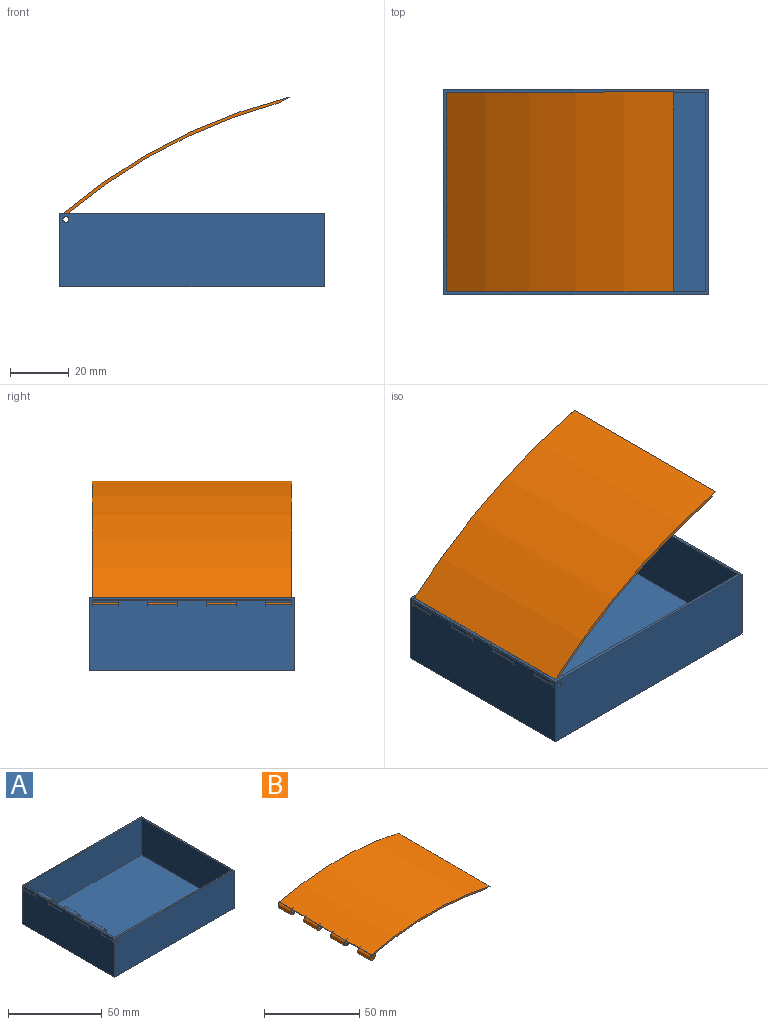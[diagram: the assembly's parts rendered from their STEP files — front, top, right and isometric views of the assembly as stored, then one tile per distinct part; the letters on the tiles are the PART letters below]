
ASSEMBLY  parts=2 mates=1
PART A: 59 faces, bbox 90x70x25 mm
  f0: plane 88x24mm, normal (0,-1,0), area 2100.9mm2, adj f1,f8,f13,f14,f20,f42,f53,f56
  f1: plane 68x20.27mm, normal (1,0,0), area 1377.8mm2, adj f0,f2,f4,f5,f6,f14,f21,f22
  f2: plane 88x24mm, normal (0,1,0), area 2100.9mm2, adj f1,f8,f13,f14,f35,f36,f52,f56
  f3: plane 70x25mm, normal (-1,0,0), area 1734.7mm2, adj f8,f10,f11,f12,f21,f22,f23,f24
  f4: cylinder r=2mm len=9.98mm, axis (0,-1,0), area 58.8mm2, adj f1,f25,f26,f33
  f5: cylinder r=2mm len=9.98mm, axis (0,-1,0), area 58.8mm2, adj f1,f23,f24,f32
  f6: cylinder r=2mm len=9.98mm, axis (0,-1,0), area 58.8mm2, adj f1,f21,f22,f34
  f7: cylinder r=1mm len=2mm, axis (0,-1,0), area 6.2mm2, adj f10,f27
  f8: plane 90x70mm, normal (0,0,1), area 312.2mm2, adj f0,f2,f3,f9,f10,f11,f19,f20
  f9: plane 70x25mm, normal (1,0,0), area 1750mm2, adj f8,f10,f11,f12
  f10: plane 90x25mm, normal (0,1,0), area 2246.9mm2, adj f3,f7,f8,f9,f12
  f11: plane 90x25mm, normal (0,-1,0), area 2246.9mm2, adj f3,f8,f9,f12,f15
  f12: plane 90x70mm, normal (0,0,-1), area 6300mm2, adj f3,f9,f10,f11
  f13: plane 68x23.99mm, normal (-1,0,0), area 1631.3mm2, adj f0,f2,f14,f56
  f14: plane 88x68mm, normal (0,0,1), area 5984mm2, adj f0,f1,f2,f13
  f15: cylinder r=1mm len=2mm, axis (0,-1,0), area 6.2mm2, adj f11,f28
  f16: cylinder r=1.99mm len=9.98mm, axis (0,1,0), area 24.1mm2, adj f21,f22,f29,f34
  f17: cylinder r=1.99mm len=9.98mm, axis (0,1,0), area 24.1mm2, adj f23,f24,f31,f32
  f18: cylinder r=1.99mm len=9.98mm, axis (0,1,0), area 24.1mm2, adj f25,f26,f30,f33
  f19: plane 68.02x0.23mm, normal (0.97,0,0.23), area 3mm2, adj f8,f27,f28,f37,f43,f49,f50,f51
  f20: cylinder r=188.99mm len=2.26mm, axis (0,1,0), area 0mm2, adj f0,f8,f27,f42
  f21: plane 4x3.99mm, normal (0,1,0), area 9.4mm2, adj f1,f3,f6,f16,f29,f34,f42,f43
  f22: plane 4x3.99mm, normal (0,-1,0), area 9.4mm2, adj f1,f3,f6,f16,f29,f34,f38,f39
  f23: plane 4x3.99mm, normal (0,1,0), area 9.4mm2, adj f1,f3,f5,f17,f31,f32,f40,f41
  f24: plane 4x3.99mm, normal (0,-1,0), area 9.4mm2, adj f1,f3,f5,f17,f31,f32,f36,f37
  f25: plane 4x3.99mm, normal (0,1,0), area 9.4mm2, adj f1,f3,f4,f18,f30,f33,f38,f39
  f26: plane 4x3.99mm, normal (0,-1,0), area 9.4mm2, adj f1,f3,f4,f18,f30,f33,f40,f41
  f27: plane 5.59x4.01mm, normal (0,-1,0), area 10.4mm2, adj f3,f7,f8,f19,f20,f42,f43
  f28: plane 5.59x4.01mm, normal (0,1,0), area 10.4mm2, adj f3,f8,f15,f19,f35,f36,f37
  f29: plane 9.98x0.01mm, normal (0.97,0,0.23), area 0.1mm2, adj f16,f21,f22,f46
  f30: plane 9.98x0.01mm, normal (0.97,0,0.23), area 0.1mm2, adj f18,f25,f26,f47
  f31: plane 9.98x0.01mm, normal (0.97,0,0.23), area 0.1mm2, adj f17,f23,f24,f48
  f32: cylinder r=188.99mm len=9.98mm, axis (0,1,0), area 0.1mm2, adj f5,f17,f23,f24
  f33: cylinder r=188.99mm len=9.98mm, axis (0,1,0), area 0.1mm2, adj f4,f18,f25,f26
  f34: cylinder r=188.99mm len=9.98mm, axis (0,1,0), area 0.1mm2, adj f6,f16,f21,f22
  f35: cylinder r=188.99mm len=2.26mm, axis (0,1,0), area 0mm2, adj f2,f8,f28,f36
  f36: cylinder r=2.01mm len=9.02mm, axis (0,-1,0), area 17.3mm2, adj f1,f2,f3,f24,f28,f35
  f37: cylinder r=2.01mm len=9.02mm, axis (0,-1,0), area 17.2mm2, adj f3,f19,f24,f28,f49,f50
  f38: cylinder r=2.01mm len=10.02mm, axis (0,-1,0), area 19.1mm2, adj f1,f3,f22,f25
  f39: cylinder r=2.01mm len=10.02mm, axis (0,-1,0), area 19.1mm2, adj f3,f22,f25,f50
  f40: cylinder r=2.01mm len=10.02mm, axis (0,-1,0), area 19.1mm2, adj f1,f3,f23,f26
  f41: cylinder r=2.01mm len=10.02mm, axis (0,-1,0), area 19.1mm2, adj f3,f23,f26,f50
  f42: cylinder r=2.01mm len=9.02mm, axis (0,-1,0), area 17.3mm2, adj f0,f1,f3,f20,f21,f27
  f43: cylinder r=2.01mm len=9.02mm, axis (0,-1,0), area 17.2mm2, adj f3,f19,f21,f27,f50,f51
  f44: cylinder r=1mm len=9.98mm, axis (0,-1,0), area 62.7mm2, adj f23,f24
  f45: cylinder r=1mm len=9.98mm, axis (0,-1,0), area 62.7mm2, adj f25,f26
  f46: cylinder r=2mm len=9.98mm, axis (0,-1,0), area 0.5mm2, adj f21,f22,f29,f50
  f47: cylinder r=2mm len=9.98mm, axis (0,-1,0), area 0.5mm2, adj f25,f26,f30,f50
  f48: cylinder r=2mm len=9.98mm, axis (0,-1,0), area 0.5mm2, adj f23,f24,f31,f50
  f49: plane 0.21x0.05mm, normal (0,1,0), area 0mm2, adj f19,f37,f50
  f50: plane 68x0.22mm, normal (1,0,0), area 14.8mm2, adj f19,f21,f22,f23,f24,f25,f26,f37
  f51: plane 0.21x0.05mm, normal (0,-1,0), area 0mm2, adj f19,f43,f50
  f52: cylinder r=188.99mm len=0.05mm, axis (0,1,0), area 0mm2, adj f2,f8,f54,f56
  f53: cylinder r=188.99mm len=0.05mm, axis (0,1,0), area 0mm2, adj f0,f8,f55,f56
  f54: plane 4.67x0.01mm, normal (0,1,0), area 0mm2, adj f8,f52,f56,f57
  f55: plane 4.67x0.01mm, normal (0,-1,0), area 0mm2, adj f8,f53,f56,f57
  f56: plane 68.02x4.63mm, normal (0,0,1), area 5.9mm2, adj f0,f2,f13,f52,f53,f54,f55,f57
  f57: cylinder r=190.01mm len=68.02mm, axis (0,1,0), area 2.9mm2, adj f8,f54,f55,f56
  f58: cylinder r=1mm len=9.98mm, axis (0,-1,0), area 62.7mm2, adj f21,f22
PART B: 23 faces, bbox 89x68x9.2 mm
  f0: cylinder r=2mm len=9mm, axis (0,-1,0), area 91.4mm2, adj f4,f5,f8,f21
  f1: cylinder r=2mm len=10mm, axis (0,-1,0), area 101.5mm2, adj f4,f5,f13,f18
  f2: cylinder r=2mm len=10mm, axis (0,-1,0), area 101.5mm2, adj f4,f5,f14,f20
  f3: cylinder r=1mm len=9mm, axis (0,-1,0), area 56.5mm2, adj f8,f21
  f4: cylinder r=189mm len=81.15mm, axis (0,1,0), area 5561.4mm2, adj f0,f1,f2,f6,f7,f8,f10,f12
  f5: plane 68x0.24mm, normal (-0.97,0,-0.23), area 16.5mm2, adj f0,f1,f2,f6,f8,f9,f10,f12
  f6: plane 89x9.17mm, normal (0,-1,0), area 94.5mm2, adj f4,f5,f7,f9,f10,f11
  f7: plane 68x4.54mm, normal (0,0,-1), area 308.8mm2, adj f4,f6,f8,f9
  f8: plane 89x9.17mm, normal (0,1,0), area 94.5mm2, adj f0,f3,f4,f5,f7,f9
  f9: cylinder r=190mm len=88mm, axis (0,1,0), area 6038.8mm2, adj f5,f6,f7,f8
  f10: cylinder r=2mm len=9mm, axis (0,-1,0), area 91.4mm2, adj f4,f5,f6,f17
  f11: cylinder r=1mm len=9mm, axis (0,-1,0), area 56.5mm2, adj f6,f17
  f12: cylinder r=2mm len=10mm, axis (0,1,0), area 24.1mm2, adj f4,f5,f13,f14
  f13: plane 4x4mm, normal (0,1,0), area 9.4mm2, adj f1,f12,f15
  f14: plane 4x4mm, normal (0,-1,0), area 9.4mm2, adj f2,f12,f22
  f15: cylinder r=1mm len=10mm, axis (0,-1,0), area 62.8mm2, adj f13,f18
  f16: cylinder r=2mm len=10mm, axis (0,1,0), area 24.1mm2, adj f4,f5,f17,f18
  f17: plane 4x4mm, normal (0,1,0), area 9.4mm2, adj f10,f11,f16
  f18: plane 4x4mm, normal (0,-1,0), area 9.4mm2, adj f1,f15,f16
  f19: cylinder r=2mm len=10mm, axis (0,1,0), area 24.1mm2, adj f4,f5,f20,f21
  f20: plane 4x4mm, normal (0,1,0), area 9.4mm2, adj f2,f19,f22
  f21: plane 4x4mm, normal (0,-1,0), area 9.4mm2, adj f0,f3,f19
  f22: cylinder r=1mm len=10mm, axis (0,-1,0), area 62.8mm2, adj f14,f20
PLACE A t=(-21.69,52.06,-10.44)mm fixed
PLACE B rot(axis=(0,-1,0),27.3deg) t=(-15.93,52.06,11.88)mm
MATE revolute B.f0 <-> A.f4  axis (0,-1,0) through (-64.69,18.06,12.56)mm
